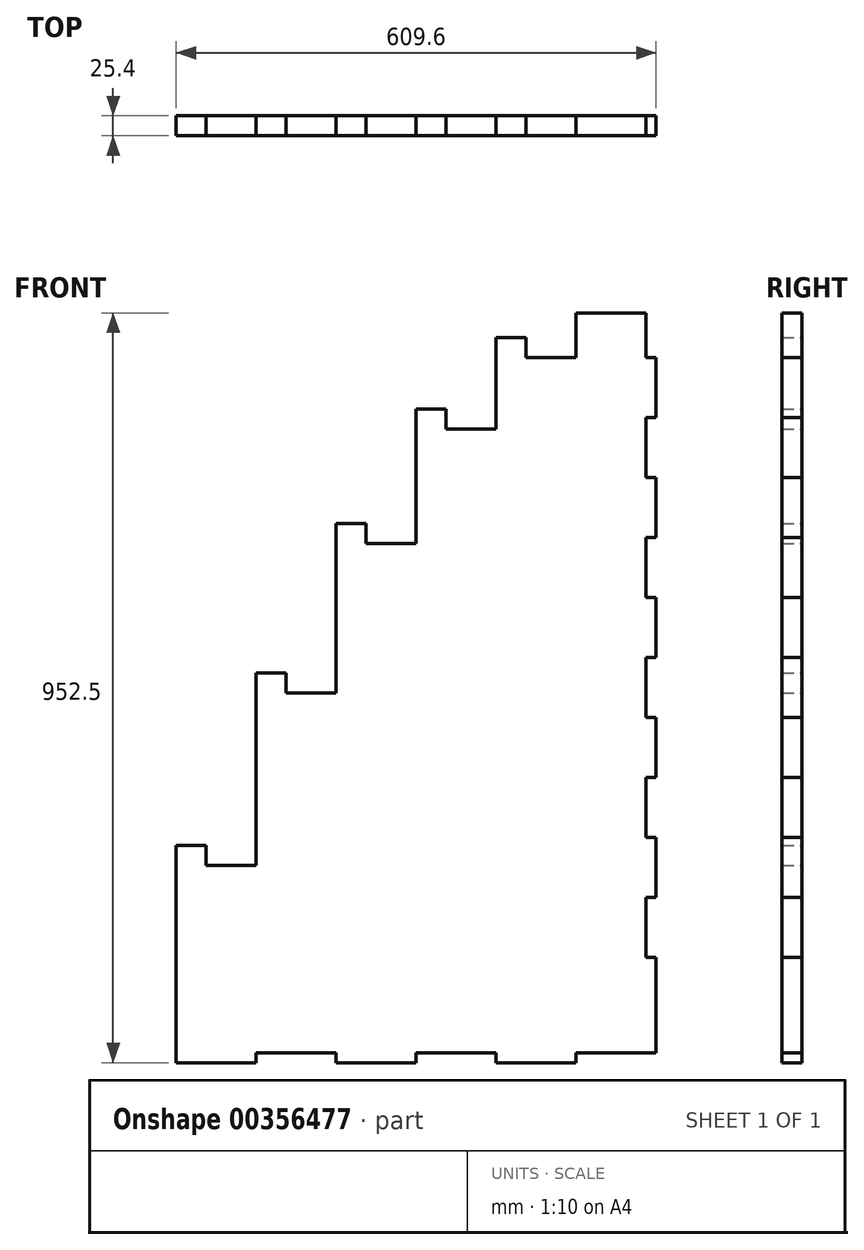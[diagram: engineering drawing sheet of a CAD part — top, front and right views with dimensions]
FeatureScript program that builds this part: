
annotation { "Feature Type Name" : "Feature", "Feature Type Description" : "" }
export const myFeature = defineFeature(function(context is Context, id is Id, definition is map)
    precondition{}
    {
        {
            var Q0;
            Q0=qCreatedBy(makeId("Front.planeOp"),FACE);
            var sketch = newSketch(context, id + "F0", { "sketchPlane" : qUnion([Q0])});
            skLineSegment(sketch, "E0", {"start": v(-252.77, -61.62) * mm, "end": v(255.23, -61.62) * mm});
            skLineSegment(sketch, "E1", {"start": v(-252.77, -61.62) * mm, "end": v(-252.77, 176.38) * mm});
            skLineSegment(sketch, "E2", {"start": v(-252.77, 176.38) * mm, "end": v(-151.17, 176.38) * mm});
            skLineSegment(sketch, "E3", {"start": v(-151.17, 176.38) * mm, "end": v(-151.17, -61.62) * mm});
            skLineSegment(sketch, "E4", {"start": v(-151.17, -61.62) * mm, "end": v(-151.17, 395.58) * mm});
            skLineSegment(sketch, "E5", {"start": v(-151.17, 395.58) * mm, "end": v(-49.57, 395.58) * mm});
            skLineSegment(sketch, "E6", {"start": v(-49.57, 395.58) * mm, "end": v(-49.57, -61.62) * mm});
            skLineSegment(sketch, "E7", {"start": v(-49.57, -61.62) * mm, "end": v(-49.57, 585.07) * mm});
            skLineSegment(sketch, "E8", {"start": v(-49.57, 585.07) * mm, "end": v(52.03, 585.07) * mm});
            skLineSegment(sketch, "E9", {"start": v(52.03, 585.07) * mm, "end": v(52.03, -61.62) * mm});
            skLineSegment(sketch, "E10", {"start": v(52.03, -61.62) * mm, "end": v(52.03, 730.36) * mm});
            skLineSegment(sketch, "E11", {"start": v(52.03, 730.36) * mm, "end": v(153.63, 730.36) * mm});
            skLineSegment(sketch, "E12", {"start": v(153.63, 730.36) * mm, "end": v(153.63, -61.62) * mm});
            skLineSegment(sketch, "E13", {"start": v(153.63, -61.62) * mm, "end": v(153.63, 821.54) * mm});
            skLineSegment(sketch, "E14", {"start": v(153.63, 821.54) * mm, "end": v(255.23, 821.54) * mm});
            skLineSegment(sketch, "E15", {"start": v(255.23, 821.54) * mm, "end": v(255.23, -61.62) * mm});
            skLineSegment(sketch, "E16.bottom", {"start": v(-252.77, 176.38) * mm, "end": v(-214.67, 176.38) * mm});
            skLineSegment(sketch, "E16.top", {"start": v(-252.77, 201.78) * mm, "end": v(-214.67, 201.78) * mm});
            skLineSegment(sketch, "E16.left", {"start": v(-252.77, 176.38) * mm, "end": v(-252.77, 201.78) * mm});
            skLineSegment(sketch, "E16.right", {"start": v(-214.67, 176.38) * mm, "end": v(-214.67, 201.78) * mm});
            skLineSegment(sketch, "E17.bottom", {"start": v(255.23, -61.62) * mm, "end": v(344.13, -61.62) * mm});
            skLineSegment(sketch, "E17.top", {"start": v(255.23, 852.78) * mm, "end": v(344.13, 852.78) * mm});
            skLineSegment(sketch, "E17.left", {"start": v(255.23, -61.62) * mm, "end": v(255.23, 852.78) * mm});
            skLineSegment(sketch, "E17.right", {"start": v(344.13, -61.62) * mm, "end": v(344.13, 852.78) * mm});
            skLineSegment(sketch, "E18.bottom", {"start": v(-151.17, 395.58) * mm, "end": v(-113.07, 395.58) * mm});
            skLineSegment(sketch, "E18.top", {"start": v(-151.17, 420.98) * mm, "end": v(-113.07, 420.98) * mm});
            skLineSegment(sketch, "E18.left", {"start": v(-151.17, 395.58) * mm, "end": v(-151.17, 420.98) * mm});
            skLineSegment(sketch, "E18.right", {"start": v(-113.07, 395.58) * mm, "end": v(-113.07, 420.98) * mm});
            skLineSegment(sketch, "E19.bottom", {"start": v(-49.57, 585.07) * mm, "end": v(-11.47, 585.07) * mm});
            skLineSegment(sketch, "E19.top", {"start": v(-49.57, 610.47) * mm, "end": v(-11.47, 610.47) * mm});
            skLineSegment(sketch, "E19.left", {"start": v(-49.57, 585.07) * mm, "end": v(-49.57, 610.47) * mm});
            skLineSegment(sketch, "E19.right", {"start": v(-11.47, 585.07) * mm, "end": v(-11.47, 610.47) * mm});
            skLineSegment(sketch, "E20.bottom", {"start": v(52.03, 730.36) * mm, "end": v(90.13, 730.36) * mm});
            skLineSegment(sketch, "E20.top", {"start": v(52.03, 755.76) * mm, "end": v(90.13, 755.76) * mm});
            skLineSegment(sketch, "E20.left", {"start": v(52.03, 730.36) * mm, "end": v(52.03, 755.76) * mm});
            skLineSegment(sketch, "E20.right", {"start": v(90.13, 730.36) * mm, "end": v(90.13, 755.76) * mm});
            skLineSegment(sketch, "E21.bottom", {"start": v(153.63, 821.54) * mm, "end": v(191.73, 821.54) * mm});
            skLineSegment(sketch, "E21.top", {"start": v(153.63, 846.94) * mm, "end": v(191.73, 846.94) * mm});
            skLineSegment(sketch, "E21.left", {"start": v(153.63, 821.54) * mm, "end": v(153.63, 846.94) * mm});
            skLineSegment(sketch, "E21.right", {"start": v(191.73, 821.54) * mm, "end": v(191.73, 846.94) * mm});
            skLineSegment(sketch, "E22.bottom", {"start": v(255.23, 852.78) * mm, "end": v(293.33, 852.78) * mm});
            skLineSegment(sketch, "E22.top", {"start": v(255.23, 878.18) * mm, "end": v(293.33, 878.18) * mm});
            skLineSegment(sketch, "E22.left", {"start": v(255.23, 852.78) * mm, "end": v(255.23, 878.18) * mm});
            skLineSegment(sketch, "E23.bottom", {"start": v(344.13, -61.62) * mm, "end": v(356.83, -61.62) * mm});
            skLineSegment(sketch, "E23.top", {"start": v(344.13, 59.54) * mm, "end": v(356.83, 59.54) * mm});
            skLineSegment(sketch, "E23.left", {"start": v(344.13, -61.62) * mm, "end": v(344.13, 59.54) * mm});
            skLineSegment(sketch, "E23.right", {"start": v(356.83, -61.62) * mm, "end": v(356.83, 59.54) * mm});
            skLineSegment(sketch, "E24.bottom", {"start": v(356.83, 135.74) * mm, "end": v(344.13, 135.74) * mm});
            skLineSegment(sketch, "E24.top", {"start": v(356.83, 211.94) * mm, "end": v(344.13, 211.94) * mm});
            skLineSegment(sketch, "E24.left", {"start": v(356.83, 135.74) * mm, "end": v(356.83, 211.94) * mm});
            skLineSegment(sketch, "E24.right", {"start": v(344.13, 135.74) * mm, "end": v(344.13, 211.94) * mm});
            skLineSegment(sketch, "E25.bottom", {"start": v(356.83, 288.14) * mm, "end": v(344.13, 288.14) * mm});
            skLineSegment(sketch, "E25.top", {"start": v(356.83, 364.34) * mm, "end": v(344.13, 364.34) * mm});
            skLineSegment(sketch, "E25.left", {"start": v(356.83, 288.14) * mm, "end": v(356.83, 364.34) * mm});
            skLineSegment(sketch, "E25.right", {"start": v(344.13, 288.14) * mm, "end": v(344.13, 364.34) * mm});
            skLineSegment(sketch, "E26.bottom", {"start": v(356.83, 440.54) * mm, "end": v(344.13, 440.54) * mm});
            skLineSegment(sketch, "E26.top", {"start": v(356.83, 516.74) * mm, "end": v(344.13, 516.74) * mm});
            skLineSegment(sketch, "E26.left", {"start": v(356.83, 440.54) * mm, "end": v(356.83, 516.74) * mm});
            skLineSegment(sketch, "E26.right", {"start": v(344.13, 440.54) * mm, "end": v(344.13, 516.74) * mm});
            skLineSegment(sketch, "E27.bottom", {"start": v(356.83, 592.94) * mm, "end": v(344.13, 592.94) * mm});
            skLineSegment(sketch, "E27.top", {"start": v(356.83, 669.14) * mm, "end": v(344.13, 669.14) * mm});
            skLineSegment(sketch, "E27.left", {"start": v(356.83, 592.94) * mm, "end": v(356.83, 669.14) * mm});
            skLineSegment(sketch, "E27.right", {"start": v(344.13, 592.94) * mm, "end": v(344.13, 669.14) * mm});
            skLineSegment(sketch, "E28.bottom", {"start": v(356.83, 745.34) * mm, "end": v(344.13, 745.34) * mm});
            skLineSegment(sketch, "E28.top", {"start": v(356.83, 821.54) * mm, "end": v(344.13, 821.54) * mm});
            skLineSegment(sketch, "E28.left", {"start": v(356.83, 745.34) * mm, "end": v(356.83, 821.54) * mm});
            skLineSegment(sketch, "E28.right", {"start": v(344.13, 745.34) * mm, "end": v(344.13, 821.54) * mm});
            skLineSegment(sketch, "E29.bottom", {"start": v(-252.77, -61.62) * mm, "end": v(-151.17, -61.62) * mm});
            skLineSegment(sketch, "E29.top", {"start": v(-252.77, -74.32) * mm, "end": v(-151.17, -74.32) * mm});
            skLineSegment(sketch, "E29.left", {"start": v(-252.77, -61.62) * mm, "end": v(-252.77, -74.32) * mm});
            skLineSegment(sketch, "E29.right", {"start": v(-151.17, -61.62) * mm, "end": v(-151.17, -74.32) * mm});
            skLineSegment(sketch, "E30.bottom", {"start": v(-49.57, -74.32) * mm, "end": v(52.03, -74.32) * mm});
            skLineSegment(sketch, "E30.top", {"start": v(-49.57, -61.62) * mm, "end": v(52.03, -61.62) * mm});
            skLineSegment(sketch, "E30.left", {"start": v(-49.57, -74.32) * mm, "end": v(-49.57, -61.62) * mm});
            skLineSegment(sketch, "E30.right", {"start": v(52.03, -74.32) * mm, "end": v(52.03, -61.62) * mm});
            skLineSegment(sketch, "E31.bottom", {"start": v(153.63, -74.32) * mm, "end": v(255.23, -74.32) * mm});
            skLineSegment(sketch, "E31.top", {"start": v(153.63, -61.62) * mm, "end": v(255.23, -61.62) * mm});
            skLineSegment(sketch, "E31.left", {"start": v(153.63, -74.32) * mm, "end": v(153.63, -61.62) * mm});
            skLineSegment(sketch, "E31.right", {"start": v(255.23, -74.32) * mm, "end": v(255.23, -61.62) * mm});
            skLineSegment(sketch, "E32.bottom", {"start": v(293.33, 878.18) * mm, "end": v(344.13, 878.18) * mm});
            skLineSegment(sketch, "E32.top", {"start": v(293.33, 852.78) * mm, "end": v(344.13, 852.78) * mm});
            skLineSegment(sketch, "E32.right", {"start": v(344.13, 878.18) * mm, "end": v(344.13, 852.78) * mm});
            skSolve(sketch);
        }
        {
            var Q0;
            Q0 = qSketchRegion(id + "F0", true);
            extrude(context, id + "F1", {"entities" : qUnion([Q0]), "depth" : 25.4 * mm});
        }
    });
